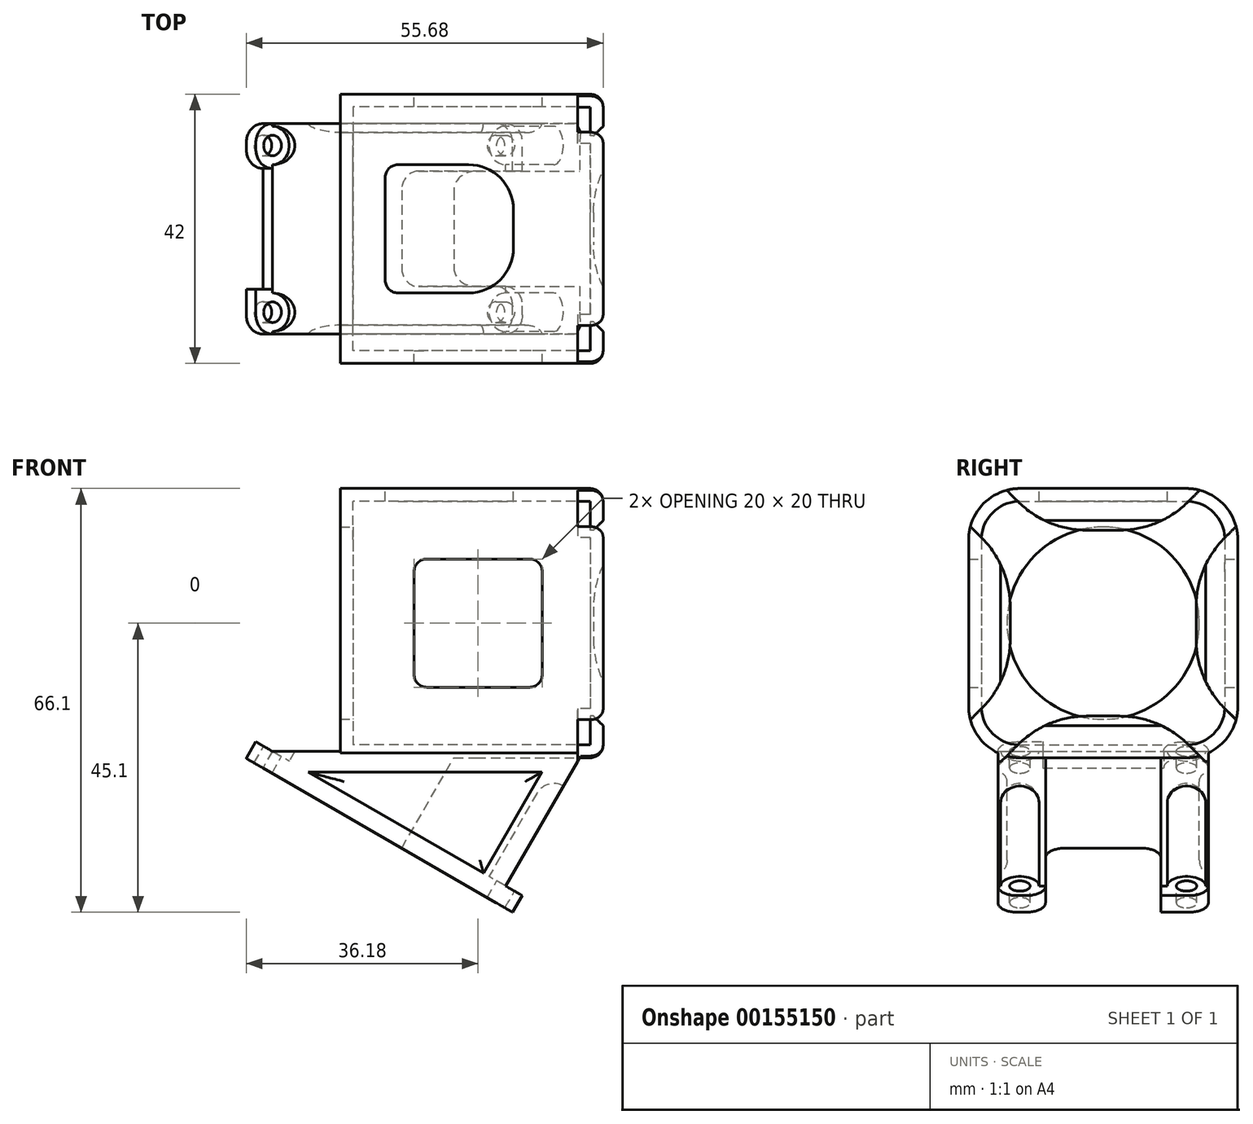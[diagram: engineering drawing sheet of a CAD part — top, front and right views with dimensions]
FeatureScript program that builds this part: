
annotation { "Feature Type Name" : "Feature", "Feature Type Description" : "" }
export const myFeature = defineFeature(function(context is Context, id is Id, definition is map)
    precondition{}
    {
        {
            var Q0;
            Q0=qCreatedBy(makeId("Right.planeOp"),FACE);
            var sketch = newSketch(context, id + "F0", { "sketchPlane" : qUnion([Q0])});
            skLineSegment(sketch, "E0.bottom", {"start": v(-13, 21) * mm, "end": v(13, 21) * mm});
            skLineSegment(sketch, "E0.top", {"start": v(-13, -21) * mm, "end": v(13, -21) * mm});
            skLineSegment(sketch, "E0.left", {"start": v(-21, 13) * mm, "end": v(-21, -13) * mm});
            skLineSegment(sketch, "E0.right", {"start": v(21, 13) * mm, "end": v(21, -13) * mm});
            skLineSegment(sketch, "E1.bottom", {"start": v(-13, 19) * mm, "end": v(13, 19) * mm});
            skLineSegment(sketch, "E1.top", {"start": v(-13, -19) * mm, "end": v(13, -19) * mm});
            skLineSegment(sketch, "E1.left", {"start": v(-19, 13) * mm, "end": v(-19, -13) * mm});
            skLineSegment(sketch, "E1.right", {"start": v(19, 13) * mm, "end": v(19, -13) * mm});
            skPoint(sketch, "E2.visualSharp", {"position": v(-19, 19) * mm});
            skArc(sketch, "E2.filletArc", {"start": v(-13, 19) * mm, "mid": v(-17.24, 17.24) * mm, "end": v(-19, 13) * mm});
            skPoint(sketch, "E3.visualSharp", {"position": v(19, 19) * mm});
            skArc(sketch, "E3.filletArc", {"start": v(19, 13) * mm, "mid": v(17.24, 17.24) * mm, "end": v(13, 19) * mm});
            skPoint(sketch, "E4.visualSharp", {"position": v(19, -19) * mm});
            skArc(sketch, "E4.filletArc", {"start": v(13, -19) * mm, "mid": v(17.24, -17.24) * mm, "end": v(19, -13) * mm});
            skPoint(sketch, "E5.visualSharp", {"position": v(-19, -19) * mm});
            skArc(sketch, "E5.filletArc", {"start": v(-19, -13) * mm, "mid": v(-17.24, -17.24) * mm, "end": v(-13, -19) * mm});
            skPoint(sketch, "E6.visualSharp", {"position": v(-21, -21) * mm});
            skArc(sketch, "E6.filletArc", {"start": v(-21, -13) * mm, "mid": v(-18.66, -18.66) * mm, "end": v(-13, -21) * mm});
            skPoint(sketch, "E7.visualSharp", {"position": v(21, -21) * mm});
            skArc(sketch, "E7.filletArc", {"start": v(13, -21) * mm, "mid": v(18.66, -18.66) * mm, "end": v(21, -13) * mm});
            skPoint(sketch, "E8.visualSharp", {"position": v(21, 21) * mm});
            skArc(sketch, "E8.filletArc", {"start": v(21, 13) * mm, "mid": v(18.66, 18.66) * mm, "end": v(13, 21) * mm});
            skPoint(sketch, "E9.visualSharp", {"position": v(-21, 21) * mm});
            skArc(sketch, "E9.filletArc", {"start": v(-13, 21) * mm, "mid": v(-18.66, 18.66) * mm, "end": v(-21, 13) * mm});
            skSolve(sketch);
        }
        {
            var Q0;
            Q0=qSketchRegion(id+"F0",true);
            extrude(context, id + "F1", {"entities" : qUnion([Q0]), "endBound" : BoundingType.SYMMETRIC, "depth" : 37 * mm});
        }
        {
            var Q0;
            Q0=makeQuery(id+"F1.opExtrude","CAP_FACE",FACE,{"disambiguationData":[OSD([sQuery(id+"F0.wireOp",EDGE,"E0.bottom"),sQuery(id+"F0.wireOp",EDGE,"E0.top"),sQuery(id+"F0.wireOp",EDGE,"E0.left"),sQuery(id+"F0.wireOp",EDGE,"E0.right"),sQuery(id+"F0.wireOp",EDGE,"E1.bottom"),sQuery(id+"F0.wireOp",EDGE,"E1.top"),sQuery(id+"F0.wireOp",EDGE,"E1.left"),sQuery(id+"F0.wireOp",EDGE,"E1.right"),sQuery(id+"F0.wireOp",EDGE,"E2.filletArc"),sQuery(id+"F0.wireOp",EDGE,"E3.filletArc"),sQuery(id+"F0.wireOp",EDGE,"E4.filletArc"),sQuery(id+"F0.wireOp",EDGE,"E5.filletArc"),sQuery(id+"F0.wireOp",EDGE,"E6.filletArc"),sQuery(id+"F0.wireOp",EDGE,"E7.filletArc"),sQuery(id+"F0.wireOp",EDGE,"E8.filletArc"),sQuery(id+"F0.wireOp",EDGE,"E9.filletArc")])],"isStart":false});
            var sketch = newSketch(context, id + "F2", { "sketchPlane" : qUnion([Q0])});
            skLineSegment(sketch, "E10.bottom", {"start": v(-12.5, 14.5) * mm, "end": v(12.5, 14.5) * mm});
            skLineSegment(sketch, "E10.top", {"start": v(-12.5, -14.5) * mm, "end": v(12.5, -14.5) * mm});
            skLineSegment(sketch, "E10.left", {"start": v(-14.5, 12.5) * mm, "end": v(-14.5, -12.5) * mm});
            skLineSegment(sketch, "E10.right", {"start": v(14.5, 12.5) * mm, "end": v(14.5, -12.5) * mm});
            skLineSegment(sketch, "E11.bottom", {"start": v(-13, 21) * mm, "end": v(13, 21) * mm});
            skLineSegment(sketch, "E11.top", {"start": v(-13, -21) * mm, "end": v(13, -21) * mm});
            skLineSegment(sketch, "E11.left", {"start": v(-21, 13) * mm, "end": v(-21, -13) * mm});
            skLineSegment(sketch, "E11.right", {"start": v(21, 13) * mm, "end": v(21, -13) * mm});
            skPoint(sketch, "E12.visualSharp", {"position": v(-21, 21) * mm});
            skArc(sketch, "E12.filletArc", {"start": v(-13, 21) * mm, "mid": v(-18.66, 18.66) * mm, "end": v(-21, 13) * mm});
            skPoint(sketch, "E13.visualSharp", {"position": v(-21, -21) * mm});
            skArc(sketch, "E13.filletArc", {"start": v(-21, -13) * mm, "mid": v(-18.66, -18.66) * mm, "end": v(-13, -21) * mm});
            skPoint(sketch, "E14.visualSharp", {"position": v(21, -21) * mm});
            skArc(sketch, "E14.filletArc", {"start": v(13, -21) * mm, "mid": v(18.66, -18.66) * mm, "end": v(21, -13) * mm});
            skPoint(sketch, "E15.visualSharp", {"position": v(21, 21) * mm});
            skArc(sketch, "E15.filletArc", {"start": v(21, 13) * mm, "mid": v(18.66, 18.66) * mm, "end": v(13, 21) * mm});
            skPoint(sketch, "E16.visualSharp", {"position": v(-14.5, 14.5) * mm});
            skArc(sketch, "E16.filletArc", {"start": v(-12.5, 14.5) * mm, "mid": v(-13.91, 13.91) * mm, "end": v(-14.5, 12.5) * mm});
            skPoint(sketch, "E17.visualSharp", {"position": v(-14.5, -14.5) * mm});
            skArc(sketch, "E17.filletArc", {"start": v(-14.5, -12.5) * mm, "mid": v(-13.91, -13.91) * mm, "end": v(-12.5, -14.5) * mm});
            skPoint(sketch, "E18.visualSharp", {"position": v(14.5, -14.5) * mm});
            skArc(sketch, "E18.filletArc", {"start": v(12.5, -14.5) * mm, "mid": v(13.91, -13.91) * mm, "end": v(14.5, -12.5) * mm});
            skPoint(sketch, "E19.visualSharp", {"position": v(14.5, 14.5) * mm});
            skArc(sketch, "E19.filletArc", {"start": v(14.5, 12.5) * mm, "mid": v(13.91, 13.91) * mm, "end": v(12.5, 14.5) * mm});
            skSolve(sketch);
        }
        {
            var Q0;
            Q0=qSketchRegion(id+"F2",true);
            extrude(context, id + "F3", {"entities" : qUnion([Q0]), "operationType" : NewBodyOperationType.ADD, "depth" : 2 * mm});
        }
        {
            var Q0;
            Q0=makeQuery(id+"F3.opExtrude","CAP_EDGE",EDGE,{"disambiguationData":[OSD([sQuery(id+"F2.wireOp",EDGE,"E10.bottom")])],"isStart":false});
            chamfer(context, id + "F4", {"entities" : qUnion([Q0]), "width" : 1.5 * mm, "tangentPropagation" : true});
        }
        {
            var Q0;
            Q0=makeQuery(id+"F3.boolean.opBoolean","MERGE",FACE,{"derivedFrom":[makeQuery(id+"F1.opExtrude","SWEPT_FACE",FACE,{"disambiguationData":[OSD([sQuery(id+"F0.wireOp",EDGE,"E0.bottom")])]}),makeQuery(id+"F3.opExtrude","SWEPT_FACE",FACE,{"disambiguationData":[OSD([sQuery(id+"F2.wireOp",EDGE,"E11.bottom")])]})]});
            var sketch = newSketch(context, id + "F5", { "sketchPlane" : qUnion([Q0])});
            skLineSegment(sketch, "E20.bottom", {"start": v(-11.5, 10) * mm, "end": v(-0.5, 10) * mm});
            skLineSegment(sketch, "E20.top", {"start": v(-11.5, -10) * mm, "end": v(-0.5, -10) * mm});
            skLineSegment(sketch, "E20.left", {"start": v(-13.5, 8) * mm, "end": v(-13.5, -8) * mm});
            skLineSegment(sketch, "E20.right", {"start": v(6.5, 3) * mm, "end": v(6.5, -3) * mm});
            skPoint(sketch, "E21.visualSharp", {"position": v(-13.5, 10) * mm});
            skArc(sketch, "E21.filletArc", {"start": v(-11.5, 10) * mm, "mid": v(-12.91, 9.41) * mm, "end": v(-13.5, 8) * mm});
            skPoint(sketch, "E22.visualSharp", {"position": v(-13.5, -10) * mm});
            skArc(sketch, "E22.filletArc", {"start": v(-13.5, -8) * mm, "mid": v(-12.91, -9.41) * mm, "end": v(-11.5, -10) * mm});
            skPoint(sketch, "E23.visualSharp", {"position": v(6.5, 10) * mm});
            skArc(sketch, "E23.filletArc", {"start": v(6.5, 3) * mm, "mid": v(4.45, 7.95) * mm, "end": v(-0.5, 10) * mm});
            skPoint(sketch, "E24.visualSharp", {"position": v(6.5, -10) * mm});
            skArc(sketch, "E24.filletArc", {"start": v(-0.5, -10) * mm, "mid": v(4.45, -7.95) * mm, "end": v(6.5, -3) * mm});
            skSolve(sketch);
        }
        {
            var Q0;
            Q0=qSketchRegion(id+"F5",true);
            extrude(context, id + "F6", {"entities" : qUnion([Q0]), "operationType" : NewBodyOperationType.REMOVE, "oppositeDirection" : true, "depth" : 5 * mm});
        }
        {
            var Q0;
            Q0=makeQuery(id+"FQ1qK5sh2A2561Q_1.boolean.opBoolean","SPLIT",FACE,{"disambiguationData":[TD([makeQuery(id+"FQ1qK5sh2A2561Q_1.opExtrude","SWEPT_FACE",FACE,{"disambiguationData":[OSD([sQuery(id+"FQFmZXkJq8ZXHcN_1.wireOp",EDGE,"qFrPXOmX-EjTA-9c1T-DURF-cY88S9PAYqbr")])]})])],"derivedFrom":makeQuery(id+"F3.boolean.opBoolean","MERGE",FACE,{"derivedFrom":[makeQuery(id+"F1.opExtrude","SWEPT_FACE",FACE,{"disambiguationData":[OSD([sQuery(id+"F0.wireOp",EDGE,"E0.top")])]}),makeQuery(id+"F3.opExtrude","SWEPT_FACE",FACE,{"disambiguationData":[OSD([sQuery(id+"F2.wireOp",EDGE,"E11.top")])]})]})});
            var sketch = newSketch(context, id + "F7", { "sketchPlane" : qUnion([Q0])});
            skLineSegment(sketch, "E25.bottom", {"start": v(-18.5, 7) * mm, "end": v(20.5, 7) * mm});
            skLineSegment(sketch, "E25.top", {"start": v(-18.5, -7) * mm, "end": v(20.5, -7) * mm});
            skLineSegment(sketch, "E25.left", {"start": v(-18.5, 7) * mm, "end": v(-18.5, -7) * mm});
            skLineSegment(sketch, "E25.right", {"start": v(20.5, 7) * mm, "end": v(20.5, -7) * mm});
            skSolve(sketch);
        }
        {
            var Q0;
            Q0=qSketchRegion(id+"F7",true);
            extrude(context, id + "F8", {"entities" : qUnion([Q0]), "operationType" : NewBodyOperationType.REMOVE, "depth" : 25 * mm});
        }
        {
            var Q0;
            Q0=qCreatedBy(makeId("Front.planeOp"),FACE);
            var sketch = newSketch(context, id + "F9", { "sketchPlane" : qUnion([Q0])});
            skLineSegment(sketch, "E26.bottom", {"start": v(9, 10) * mm, "end": v(-7, 10) * mm});
            skLineSegment(sketch, "E26.top", {"start": v(9, -10) * mm, "end": v(-7, -10) * mm});
            skLineSegment(sketch, "E26.left", {"start": v(11, 8) * mm, "end": v(11, -8) * mm});
            skLineSegment(sketch, "E26.right", {"start": v(-9, 8) * mm, "end": v(-9, -8) * mm});
            skPoint(sketch, "E27.visualSharp", {"position": v(11, 10) * mm});
            skArc(sketch, "E27.filletArc", {"start": v(11, 8) * mm, "mid": v(10.41, 9.41) * mm, "end": v(9, 10) * mm});
            skPoint(sketch, "E28.visualSharp", {"position": v(11, -10) * mm});
            skArc(sketch, "E28.filletArc", {"start": v(9, -10) * mm, "mid": v(10.41, -9.41) * mm, "end": v(11, -8) * mm});
            skPoint(sketch, "E29.visualSharp", {"position": v(-9, -10) * mm});
            skArc(sketch, "E29.filletArc", {"start": v(-9, -8) * mm, "mid": v(-8.41, -9.41) * mm, "end": v(-7, -10) * mm});
            skPoint(sketch, "E30.visualSharp", {"position": v(-9, 10) * mm});
            skArc(sketch, "E30.filletArc", {"start": v(-7, 10) * mm, "mid": v(-8.41, 9.41) * mm, "end": v(-9, 8) * mm});
            skSolve(sketch);
        }
        {
            var Q0;
            Q0=qSketchRegion(id+"F9",true);
            extrude(context, id + "F10", {"entities" : qUnion([Q0]), "operationType" : NewBodyOperationType.REMOVE, "endBound" : BoundingType.SYMMETRIC, "depth" : 45 * mm});
        }
        {
            var Q0;
            Q0=makeQuery(id+"F1.opExtrude","CAP_FACE",FACE,{"disambiguationData":[OSD([sQuery(id+"F0.wireOp",EDGE,"E0.bottom"),sQuery(id+"F0.wireOp",EDGE,"E0.top"),sQuery(id+"F0.wireOp",EDGE,"E0.left"),sQuery(id+"F0.wireOp",EDGE,"E0.right"),sQuery(id+"F0.wireOp",EDGE,"E1.bottom"),sQuery(id+"F0.wireOp",EDGE,"E1.top"),sQuery(id+"F0.wireOp",EDGE,"E1.left"),sQuery(id+"F0.wireOp",EDGE,"E1.right"),sQuery(id+"F0.wireOp",EDGE,"E2.filletArc"),sQuery(id+"F0.wireOp",EDGE,"E3.filletArc"),sQuery(id+"F0.wireOp",EDGE,"E4.filletArc"),sQuery(id+"F0.wireOp",EDGE,"E5.filletArc"),sQuery(id+"F0.wireOp",EDGE,"E6.filletArc"),sQuery(id+"F0.wireOp",EDGE,"E7.filletArc"),sQuery(id+"F0.wireOp",EDGE,"E8.filletArc"),sQuery(id+"F0.wireOp",EDGE,"E9.filletArc")])],"isStart":true});
            var sketch = newSketch(context, id + "F11", { "sketchPlane" : qUnion([Q0])});
            skLineSegment(sketch, "E31.bottom", {"start": v(-13, 21) * mm, "end": v(13, 21) * mm});
            skLineSegment(sketch, "E31.top", {"start": v(-13, -21) * mm, "end": v(13, -21) * mm});
            skLineSegment(sketch, "E31.left", {"start": v(-21, 13) * mm, "end": v(-21, -13) * mm});
            skLineSegment(sketch, "E31.right", {"start": v(21, 13) * mm, "end": v(21, -13) * mm});
            skPoint(sketch, "E32.visualSharp", {"position": v(-21, 21) * mm});
            skArc(sketch, "E32.filletArc", {"start": v(-13, 21) * mm, "mid": v(-18.66, 18.66) * mm, "end": v(-21, 13) * mm});
            skPoint(sketch, "E33.visualSharp", {"position": v(21, 21) * mm});
            skArc(sketch, "E33.filletArc", {"start": v(21, 13) * mm, "mid": v(18.66, 18.66) * mm, "end": v(13, 21) * mm});
            skPoint(sketch, "E34.visualSharp", {"position": v(21, -21) * mm});
            skArc(sketch, "E34.filletArc", {"start": v(13, -21) * mm, "mid": v(18.66, -18.66) * mm, "end": v(21, -13) * mm});
            skPoint(sketch, "E35.visualSharp", {"position": v(-21, -21) * mm});
            skArc(sketch, "E35.filletArc", {"start": v(-21, -13) * mm, "mid": v(-18.66, -18.66) * mm, "end": v(-13, -21) * mm});
            skCircle(sketch, "E36", {"center": v(0, 0) * mm, "radius": 15 * mm});
            skSolve(sketch);
        }
        {
            var Q0;
            Q0 = qSketchRegion(id + "F11", true);
            extrude(context, id + "F12", {"entities" : qUnion([Q0]), "operationType" : NewBodyOperationType.ADD, "depth" : 2 * mm});
        }
        {
            var Q0;
            Q0=qCreatedBy(makeId("Front.planeOp"),FACE);
            var sketch = newSketch(context, id + "F13", { "sketchPlane" : qUnion([Q0])});
            skLineSegment(sketch, "E37", {"start": v(7.89, -42.5) * mm, "end": v(5.3, -41) * mm});
            skLineSegment(sketch, "E38", {"start": v(-33.68, -18.5) * mm, "end": v(-35.18, -21.1) * mm});
            skLineSegment(sketch, "E39", {"start": v(-35.18, -21.1) * mm, "end": v(6.39, -45.1) * mm});
            skLineSegment(sketch, "E40", {"start": v(6.39, -45.1) * mm, "end": v(7.89, -42.5) * mm});
            skLineSegment(sketch, "E41.trimOffspring", {"start": v(-31.08, -20) * mm, "end": v(-33.68, -18.5) * mm});
            skLineSegment(sketch, "E42", {"start": v(5.3, -41) * mm, "end": v(17.41, -20) * mm});
            skLineSegment(sketch, "E43", {"start": v(-20.5, -20) * mm, "end": v(-31.08, -20) * mm});
            skLineSegment(sketch, "E44", {"start": v(-20.5, -20) * mm, "end": v(17.41, -20) * mm});
            skSolve(sketch);
        }
        {
            var Q0;
            Q0=makeQuery(id+"F13.imprint","IMPRINT",FACE,{"disambiguationData":[TD([[makeQuery(id+"F13.imprint","IMPRINT",EDGE,{"derivedFrom":sQuery(id+"F13.wireOp",EDGE,"E37")}),1.0]])]});
            extrude(context, id + "F14", {"entities" : qUnion([Q0]), "operationType" : NewBodyOperationType.ADD, "endBound" : BoundingType.SYMMETRIC, "depth" : 32.84 * mm});
        }
        {
            var Q0;
            Q0=makeQuery(id+"F14.opExtrude","SWEPT_FACE",FACE,{"disambiguationData":[OSD([sQuery(id+"F13.wireOp",EDGE,"E37")])]});
            var sketch = newSketch(context, id + "F15", { "sketchPlane" : qUnion([Q0])});
            skCircle(sketch, "E45", {"center": v(25.08, -13) * mm, "radius": 1.6 * mm});
            skCircle(sketch, "E46", {"center": v(25.08, 13) * mm, "radius": 1.6 * mm});
            skCircle(sketch, "E47", {"center": v(-16.92, -13) * mm, "radius": 1.6 * mm});
            skCircle(sketch, "E48", {"center": v(-16.92, 13) * mm, "radius": 1.6 * mm});
            skSolve(sketch);
        }
        {
            var Q0;
            Q0=makeQuery(id+"F14.opExtrude","SWEPT_FACE",FACE,{"disambiguationData":[OSD([sQuery(id+"F13.wireOp",EDGE,"E39")])]});
            var sketch = newSketch(context, id + "F16", { "sketchPlane" : qUnion([Q0])});
            skLineSegment(sketch, "E49.bottom", {"start": v(-19.92, 9.42) * mm, "end": v(-16.92, 9.42) * mm});
            skLineSegment(sketch, "E49.top", {"start": v(-19.92, -9.42) * mm, "end": v(-16.92, -9.42) * mm});
            skLineSegment(sketch, "E49.left", {"start": v(-19.92, 9.42) * mm, "end": v(-19.92, -9.42) * mm});
            skLineSegment(sketch, "E49.right", {"start": v(-16.92, 9.42) * mm, "end": v(-16.92, -9.42) * mm});
            skSolve(sketch);
        }
        {
            var Q0;
            Q0 = qSketchRegion(id + "F16", true);
            extrude(context, id + "F17", {"entities" : qUnion([Q0]), "operationType" : NewBodyOperationType.REMOVE, "oppositeDirection" : true, "depth" : 3.5 * mm});
        }
        {
            var Q0;
            Q0=makeQuery(id+"F14.opExtrude","CAP_EDGE",EDGE,{"disambiguationData":[OSD([sQuery(id+"F13.wireOp",EDGE,"E38")])],"isStart":true});
            var Q1;
            Q1=makeQuery(id+"F17.boolean.opBoolean","COPY",EDGE,{"derivedFrom":makeQuery(id+"F17.opExtrude","SWEPT_EDGE",EDGE,{"disambiguationData":[OSD([sQuery(id+"F13.wireOp",EDGE,"E38"),sQuery(id+"F13.wireOp",EDGE,"E39"),sQuery(id+"F16.wireOp",EDGE,"E49.top"),sQuery(id+"F16.wireOp",EDGE,"E49.left")])]})});
            var Q2;
            Q2=makeQuery(id+"F17.boolean.opBoolean","COPY",EDGE,{"derivedFrom":makeQuery(id+"F17.opExtrude","SWEPT_EDGE",EDGE,{"disambiguationData":[OSD([sQuery(id+"F13.wireOp",EDGE,"E38"),sQuery(id+"F13.wireOp",EDGE,"E39"),sQuery(id+"F16.wireOp",EDGE,"E49.bottom"),sQuery(id+"F16.wireOp",EDGE,"E49.left")])]})});
            var Q3;
            Q3=makeQuery(id+"F14.opExtrude","CAP_EDGE",EDGE,{"disambiguationData":[OSD([sQuery(id+"F13.wireOp",EDGE,"E38")])],"isStart":false});
            fillet(context, id + "F18", {"entities" : qUnion([Q0, Q1, Q2, Q3]), "radius" : 3 * mm, "tangentPropagation" : true, "allowEdgeOverflow" : false});
        }
        {
            var Q0;
            Q0=qCreatedBy(makeId("Front.planeOp"),FACE);
            var sketch = newSketch(context, id + "F19", { "sketchPlane" : qUnion([Q0])});
            skLineSegment(sketch, "E50", {"start": v(6.39, -45.1) * mm, "end": v(-10.93, -35.1) * mm});
            skLineSegment(sketch, "E51", {"start": v(-10.93, -35.1) * mm, "end": v(-2.8, -21) * mm});
            skLineSegment(sketch, "E52", {"start": v(-2.8, -21) * mm, "end": v(20.3, -21) * mm});
            skLineSegment(sketch, "E53", {"start": v(20.3, -21) * mm, "end": v(6.39, -45.1) * mm});
            skSolve(sketch);
        }
        {
            var Q0;
            Q0=makeQuery(id+"F19.imprint","IMPRINT",FACE,{"disambiguationData":[TD([[makeQuery(id+"F19.imprint","IMPRINT",EDGE,{"derivedFrom":sQuery(id+"F19.wireOp",EDGE,"E50")}),-1.0]])]});
            extrude(context, id + "F20", {"entities" : qUnion([Q0]), "operationType" : NewBodyOperationType.REMOVE, "endBound" : BoundingType.SYMMETRIC, "oppositeDirection" : true, "depth" : 18 * mm});
        }
        {
            var Q0;
            Q0=makeQuery(id+"F20.boolean.opBoolean","COPY",EDGE,{"derivedFrom":makeQuery(id+"F20.opExtrude","CAP_EDGE",EDGE,{"disambiguationData":[OSD([sQuery(id+"F19.wireOp",EDGE,"E51")])],"isStart":false})});
            var Q1;
            Q1=makeQuery(id+"F20.boolean.opBoolean","COPY",EDGE,{"derivedFrom":makeQuery(id+"F20.opExtrude","CAP_EDGE",EDGE,{"disambiguationData":[OSD([sQuery(id+"F19.wireOp",EDGE,"E51")])],"isStart":true})});
            fillet(context, id + "F21", {"entities" : qUnion([Q0, Q1]), "radius" : 3 * mm, "tangentPropagation" : true, "allowEdgeOverflow" : false});
        }
        {
            var Q0;
            Q0 = qSketchRegion(id + "F15", true);
            extrude(context, id + "F22", {"entities" : qUnion([Q0]), "operationType" : NewBodyOperationType.REMOVE, "endBound" : BoundingType.SYMMETRIC, "oppositeDirection" : true, "depth" : 25 * mm});
        }
        {
            var Q0;
            {var subQ1=sQuery(id+"F13.wireOp",EDGE,"E41.trimOffspring");Q0=makeQuery(id+"F17.boolean.opBoolean","SPLIT",FACE,{"disambiguationData":[TD([makeQuery(id+"F17.opExtrude","SWEPT_FACE",FACE,{"disambiguationData":[OSD([sQuery(id+"F16.wireOp",EDGE,"E49.bottom")])]})])],"derivedFrom":makeQuery(id+"F14.opExtrude","SWEPT_FACE",FACE,{"disambiguationData":[OSD([subQ1])]})});}
            var sketch = newSketch(context, id + "F23", { "sketchPlane" : qUnion([Q0])});
            skCircle(sketch, "E54", {"center": v(-16.92, -13) * mm, "radius": 3 * mm});
            skCircle(sketch, "E55", {"center": v(25.08, -13) * mm, "radius": 3 * mm});
            skPoint(sketch, "E55.centerSnap0", {"position": v(-15.32, -13) * mm});
            skPoint(sketch, "E56.MirrorP", {"position": v(-15.32, 13) * mm});
            skCircle(sketch, "E57.MirrorC", {"center": v(-16.92, 13) * mm, "radius": 3 * mm});
            skCircle(sketch, "E58.MirrorC", {"center": v(25.08, 13) * mm, "radius": 3 * mm});
            skSolve(sketch);
        }
        {
            var Q0;
            Q0 = qSketchRegion(id + "F23", true);
            var Q1;
            Q1=makeQuery(id+"F12.boolean.opBoolean","MERGE",FACE,{"derivedFrom":[makeQuery(id+"F3.boolean.opBoolean","MERGE",FACE,{"derivedFrom":[makeQuery(id+"F1.opExtrude","SWEPT_FACE",FACE,{"disambiguationData":[OSD([sQuery(id+"F0.wireOp",EDGE,"E6.filletArc")])]}),makeQuery(id+"F3.opExtrude","SWEPT_FACE",FACE,{"disambiguationData":[OSD([sQuery(id+"F2.wireOp",EDGE,"E13.filletArc")])]})]}),makeQuery(id+"F12.opExtrude","SWEPT_FACE",FACE,{"disambiguationData":[OSD([sQuery(id+"F11.wireOp",EDGE,"E34.filletArc")])]})]});
            extrude(context, id + "F24", {"entities" : qUnion([Q0]), "operationType" : NewBodyOperationType.REMOVE, "endBoundEntityFace" : qUnion([Q1]), "depth" : 15 * mm});
        }
        {
            var Q0;
            Q0=makeQuery(id+"F3.opExtrude","CAP_FACE",FACE,{"disambiguationData":[OSD([sQuery(id+"F2.wireOp",EDGE,"E10.bottom"),sQuery(id+"F2.wireOp",EDGE,"E10.top"),sQuery(id+"F2.wireOp",EDGE,"E10.left"),sQuery(id+"F2.wireOp",EDGE,"E10.right"),sQuery(id+"F2.wireOp",EDGE,"E11.bottom"),sQuery(id+"F2.wireOp",EDGE,"E11.top"),sQuery(id+"F2.wireOp",EDGE,"E11.left"),sQuery(id+"F2.wireOp",EDGE,"E11.right"),sQuery(id+"F2.wireOp",EDGE,"E12.filletArc"),sQuery(id+"F2.wireOp",EDGE,"E13.filletArc"),sQuery(id+"F2.wireOp",EDGE,"E14.filletArc"),sQuery(id+"F2.wireOp",EDGE,"E15.filletArc"),sQuery(id+"F2.wireOp",EDGE,"E16.filletArc"),sQuery(id+"F2.wireOp",EDGE,"E17.filletArc"),sQuery(id+"F2.wireOp",EDGE,"E18.filletArc"),sQuery(id+"F2.wireOp",EDGE,"E19.filletArc")])],"isStart":true});
            var sketch = newSketch(context, id + "F25", { "sketchPlane" : qUnion([Q0])});
            skLineSegment(sketch, "E59", {"start": v(-22.07, 16.41) * mm, "end": v(-5.66, 0) * mm});
            skLineSegment(sketch, "E60", {"start": v(-16.41, 22.07) * mm, "end": v(0, 5.66) * mm});
            skLineSegment(sketch, "E61", {"start": v(-19.45, 19.45) * mm, "end": v(13.91, -13.91) * mm, "construction": true});
            skLineSegment(sketch, "E62", {"start": v(-13.91, -13.91) * mm, "end": v(13.91, 13.91) * mm, "construction": true});
            skLineSegment(sketch, "E63", {"start": v(-22.07, -16.41) * mm, "end": v(-5.66, 0) * mm});
            skLineSegment(sketch, "E64", {"start": v(22.07, 16.41) * mm, "end": v(5.66, 0) * mm});
            skLineSegment(sketch, "E65.trimOffspring", {"start": v(0, 5.66) * mm, "end": v(16.41, 22.07) * mm});
            skLineSegment(sketch, "E66.trimOffspring", {"start": v(5.66, 0) * mm, "end": v(22.07, -16.41) * mm});
            skLineSegment(sketch, "E67.trimOffspring", {"start": v(0, -5.66) * mm, "end": v(-16.41, -22.07) * mm});
            skLineSegment(sketch, "E68.trimOffspring", {"start": v(0, -5.66) * mm, "end": v(16.41, -22.07) * mm});
            skPoint(sketch, "E69.centerSnap0", {"position": v(-2.77, 2.77) * mm});
            skArc(sketch, "E70", {"start": v(-16.41, 22.07) * mm, "mid": v(-19.45, 19.45) * mm, "end": v(-22.07, 16.41) * mm});
            skArc(sketch, "E71.trimOffspring", {"start": v(22.07, 16.41) * mm, "mid": v(19.45, 19.45) * mm, "end": v(16.41, 22.07) * mm});
            skArc(sketch, "E72.trimOffspring", {"start": v(16.41, -22.07) * mm, "mid": v(19.45, -19.45) * mm, "end": v(22.07, -16.41) * mm});
            skArc(sketch, "E73.trimOffspring", {"start": v(-22.07, -16.41) * mm, "mid": v(-19.45, -19.45) * mm, "end": v(-16.41, -22.07) * mm});
            skSolve(sketch);
        }
        {
            var Q0;
            Q0 = qSketchRegion(id + "F25", true);
            extrude(context, id + "F26", {"entities" : qUnion([Q0]), "operationType" : NewBodyOperationType.REMOVE, "oppositeDirection" : true, "depth" : 25 * mm});
        }
        {
            var Q0;
            Q0=makeQuery(id+"F3.opExtrude","CAP_EDGE",EDGE,{"disambiguationData":[OSD([sQuery(id+"F2.wireOp",EDGE,"E11.bottom")])],"isStart":false});
            var Q1;
            Q1=makeQuery(id+"F3.opExtrude","CAP_EDGE",EDGE,{"disambiguationData":[OSD([sQuery(id+"F2.wireOp",EDGE,"E11.left")])],"isStart":false});
            var Q2;
            Q2=makeQuery(id+"F3.opExtrude","CAP_EDGE",EDGE,{"disambiguationData":[OSD([sQuery(id+"F2.wireOp",EDGE,"E11.right")])],"isStart":false});
            var Q3;
            Q3=makeQuery(id+"F3.opExtrude","CAP_EDGE",EDGE,{"disambiguationData":[OSD([sQuery(id+"F2.wireOp",EDGE,"E11.top")])],"isStart":false});
            fillet(context, id + "F27", {"entities" : qUnion([Q0, Q1, Q2, Q3]), "radius" : 2 * mm, "tangentPropagation" : true, "allowEdgeOverflow" : false});
        }
        {
            var Q0;
            Q0=makeQuery(id+"F26.boolean.opBoolean","INTERSECT",EDGE,{"derivedFrom":[makeQuery(id+"F3.opExtrude","SWEPT_FACE",FACE,{"disambiguationData":[OSD([sQuery(id+"F2.wireOp",EDGE,"E10.left")])]}),makeQuery(id+"F26.opExtrude","SWEPT_FACE",FACE,{"disambiguationData":[OSD([sQuery(id+"F25.wireOp",EDGE,"E64")])]})]});
            var Q1;
            Q1=makeQuery(id+"F26.boolean.opBoolean","INTERSECT",EDGE,{"derivedFrom":[makeQuery(id+"F3.opExtrude","SWEPT_FACE",FACE,{"disambiguationData":[OSD([sQuery(id+"F2.wireOp",EDGE,"E10.bottom")])]}),makeQuery(id+"F26.opExtrude","SWEPT_FACE",FACE,{"disambiguationData":[OSD([sQuery(id+"F25.wireOp",EDGE,"E65.trimOffspring")])]})]});
            var Q2;
            Q2=makeQuery(id+"F26.boolean.opBoolean","INTERSECT",EDGE,{"derivedFrom":[makeQuery(id+"F3.opExtrude","SWEPT_FACE",FACE,{"disambiguationData":[OSD([sQuery(id+"F2.wireOp",EDGE,"E10.bottom")])]}),makeQuery(id+"F26.opExtrude","SWEPT_FACE",FACE,{"disambiguationData":[OSD([sQuery(id+"F25.wireOp",EDGE,"E60")])]})]});
            var Q3;
            Q3=makeQuery(id+"F26.boolean.opBoolean","INTERSECT",EDGE,{"derivedFrom":[makeQuery(id+"F3.opExtrude","SWEPT_FACE",FACE,{"disambiguationData":[OSD([sQuery(id+"F2.wireOp",EDGE,"E10.right")])]}),makeQuery(id+"F26.opExtrude","SWEPT_FACE",FACE,{"disambiguationData":[OSD([sQuery(id+"F25.wireOp",EDGE,"E59")])]})]});
            var Q4;
            Q4=makeQuery(id+"F26.boolean.opBoolean","INTERSECT",EDGE,{"derivedFrom":[makeQuery(id+"F3.opExtrude","SWEPT_FACE",FACE,{"disambiguationData":[OSD([sQuery(id+"F2.wireOp",EDGE,"E10.right")])]}),makeQuery(id+"F26.opExtrude","SWEPT_FACE",FACE,{"disambiguationData":[OSD([sQuery(id+"F25.wireOp",EDGE,"E63")])]})]});
            var Q5;
            Q5=makeQuery(id+"F26.boolean.opBoolean","INTERSECT",EDGE,{"derivedFrom":[makeQuery(id+"F3.opExtrude","SWEPT_FACE",FACE,{"disambiguationData":[OSD([sQuery(id+"F2.wireOp",EDGE,"E10.top")])]}),makeQuery(id+"F26.opExtrude","SWEPT_FACE",FACE,{"disambiguationData":[OSD([sQuery(id+"F25.wireOp",EDGE,"E67.trimOffspring")])]})]});
            var Q6;
            Q6=makeQuery(id+"F26.boolean.opBoolean","INTERSECT",EDGE,{"derivedFrom":[makeQuery(id+"F3.opExtrude","SWEPT_FACE",FACE,{"disambiguationData":[OSD([sQuery(id+"F2.wireOp",EDGE,"E10.left")])]}),makeQuery(id+"F26.opExtrude","SWEPT_FACE",FACE,{"disambiguationData":[OSD([sQuery(id+"F25.wireOp",EDGE,"E66.trimOffspring")])]})]});
            var Q7;
            Q7=makeQuery(id+"F26.boolean.opBoolean","INTERSECT",EDGE,{"derivedFrom":[makeQuery(id+"F3.opExtrude","SWEPT_FACE",FACE,{"disambiguationData":[OSD([sQuery(id+"F2.wireOp",EDGE,"E10.top")])]}),makeQuery(id+"F26.opExtrude","SWEPT_FACE",FACE,{"disambiguationData":[OSD([sQuery(id+"F25.wireOp",EDGE,"E68.trimOffspring")])]})]});
            fillet(context, id + "F28", {"entities" : qUnion([Q0, Q1, Q2, Q3, Q4, Q5, Q6, Q7]), "radius" : 15.25 * mm, "tangentPropagation" : true, "allowEdgeOverflow" : false});
        }
        {
            var Q0;
            Q0=makeQuery(id+"F14.opExtrude","CAP_EDGE",EDGE,{"disambiguationData":[OSD([sQuery(id+"F13.wireOp",EDGE,"E40")])],"isStart":false});
            var Q1;
            Q1=makeQuery(id+"F20.boolean.opBoolean","COPY",EDGE,{"derivedFrom":makeQuery(id+"F20.opExtrude","CAP_EDGE",EDGE,{"disambiguationData":[OSD([sQuery(id+"F19.wireOp",EDGE,"E53")])],"isStart":true})});
            var Q2;
            Q2=makeQuery(id+"F20.boolean.opBoolean","COPY",EDGE,{"derivedFrom":makeQuery(id+"F20.opExtrude","CAP_EDGE",EDGE,{"disambiguationData":[OSD([sQuery(id+"F19.wireOp",EDGE,"E53")])],"isStart":false})});
            var Q3;
            Q3=makeQuery(id+"F14.opExtrude","CAP_EDGE",EDGE,{"disambiguationData":[OSD([sQuery(id+"F13.wireOp",EDGE,"E40")])],"isStart":true});
            fillet(context, id + "F29", {"entities" : qUnion([Q0, Q1, Q2, Q3]), "radius" : 3 * mm, "tangentPropagation" : true, "allowEdgeOverflow" : false});
        }
        {
            var Q0;
            Q0=makeQuery(id+"F24.boolean.opBoolean","COPY",FACE,{"derivedFrom":makeQuery(id+"F24.opExtrude","CAP_FACE",FACE,{"disambiguationData":[OSD([sQuery(id+"F23.wireOp",EDGE,"E55")])],"isStart":false})});
            var Q1;
            Q1=makeQuery(id+"F24.boolean.opBoolean","COPY",FACE,{"derivedFrom":makeQuery(id+"F24.opExtrude","CAP_FACE",FACE,{"disambiguationData":[OSD([sQuery(id+"F23.wireOp",EDGE,"E58.MirrorC")])],"isStart":false})});
            var Q2;
            {var subQ1=sQuery(id+"F13.wireOp",EDGE,"E42");Q2=makeQuery(id+"F24.boolean.opBoolean","INTERSECT",EDGE,{"derivedFrom":[makeQuery(id+"F20.boolean.opBoolean","SPLIT",FACE,{"disambiguationData":[TD([makeQuery(id+"F1.opExtrude","SWEPT_FACE",FACE,{"disambiguationData":[OSD([sQuery(id+"F0.wireOp",EDGE,"E6.filletArc")])]})])],"derivedFrom":makeQuery(id+"F14.opExtrude","SWEPT_FACE",FACE,{"disambiguationData":[OSD([subQ1])]})}),makeQuery(id+"F24.opExtrude","CAP_FACE",FACE,{"disambiguationData":[OSD([sQuery(id+"F23.wireOp",EDGE,"E55")])],"isStart":false})]});}
            revolve(context, id + "F30", {"operationType" : NewBodyOperationType.REMOVE, "entities" : qUnion([Q0, Q1]), "axis" : qUnion([Q2]), "revolveType" : RevolveType.FULL, "oppositeDirection" : true});
        }
        {
            var Q0;
            Q0 = qSketchRegion(id + "F25", true);
            extrude(context, id + "F31", {"entities" : qUnion([Q0]), "operationType" : NewBodyOperationType.REMOVE, "depth" : 2 * mm});
        }
        {
            var Q0;
            Q0=qCreatedBy(makeId("Front.planeOp"),FACE);
            var sketch = newSketch(context, id + "F32", { "sketchPlane" : qUnion([Q0])});
            skLineSegment(sketch, "E74", {"start": v(10.93, -23.23) * mm, "end": v(1.83, -39) * mm});
            skLineSegment(sketch, "E75", {"start": v(1.83, -39) * mm, "end": v(-25.48, -23.23) * mm});
            skLineSegment(sketch, "E76", {"start": v(-25.48, -23.23) * mm, "end": v(10.93, -23.23) * mm});
            skSolve(sketch);
        }
        {
            var Q0;
            Q0 = qSketchRegion(id + "F32", true);
            extrude(context, id + "F33", {"entities" : qUnion([Q0]), "operationType" : NewBodyOperationType.REMOVE, "depth" : 17 * mm, "hasSecondDirection" : true, "secondDirectionOppositeDirection" : false, "secondDirectionDepth" : 15 * mm});
        }
        {
            var Q0;
            Q0 = qSketchRegion(id + "F32", true);
            extrude(context, id + "F34", {"entities" : qUnion([Q0]), "operationType" : NewBodyOperationType.REMOVE, "oppositeDirection" : true, "depth" : 17 * mm, "hasSecondDirection" : true, "secondDirectionOppositeDirection" : true, "secondDirectionDepth" : 15 * mm});
        }
        {
            var Q0;
            Q0=makeQuery(id+"F34.boolean.opBoolean","COPY",EDGE,{"derivedFrom":makeQuery(id+"F34.opExtrude","CAP_EDGE",EDGE,{"disambiguationData":[OSD([sQuery(id+"F32.wireOp",EDGE,"E76")])],"isStart":true})});
            var Q1;
            Q1=makeQuery(id+"F34.boolean.opBoolean","COPY",EDGE,{"derivedFrom":makeQuery(id+"F34.opExtrude","CAP_EDGE",EDGE,{"disambiguationData":[OSD([sQuery(id+"F32.wireOp",EDGE,"E74")])],"isStart":true})});
            var Q2;
            Q2=makeQuery(id+"F34.boolean.opBoolean","COPY",EDGE,{"derivedFrom":makeQuery(id+"F34.opExtrude","CAP_EDGE",EDGE,{"disambiguationData":[OSD([sQuery(id+"F32.wireOp",EDGE,"E75")])],"isStart":true})});
            var Q3;
            Q3=makeQuery(id+"F33.boolean.opBoolean","COPY",FACE,{"derivedFrom":makeQuery(id+"F33.opExtrude","CAP_FACE",FACE,{"disambiguationData":[OSD([sQuery(id+"F32.wireOp",EDGE,"E74"),sQuery(id+"F32.wireOp",EDGE,"E75"),sQuery(id+"F32.wireOp",EDGE,"E76")])],"isStart":true})});
            fillet(context, id + "F35", {"entities" : qUnion([Q0, Q1, Q2, Q3]), "radius" : 1.5 * mm, "tangentPropagation" : true, "allowEdgeOverflow" : false});
        }
    });
